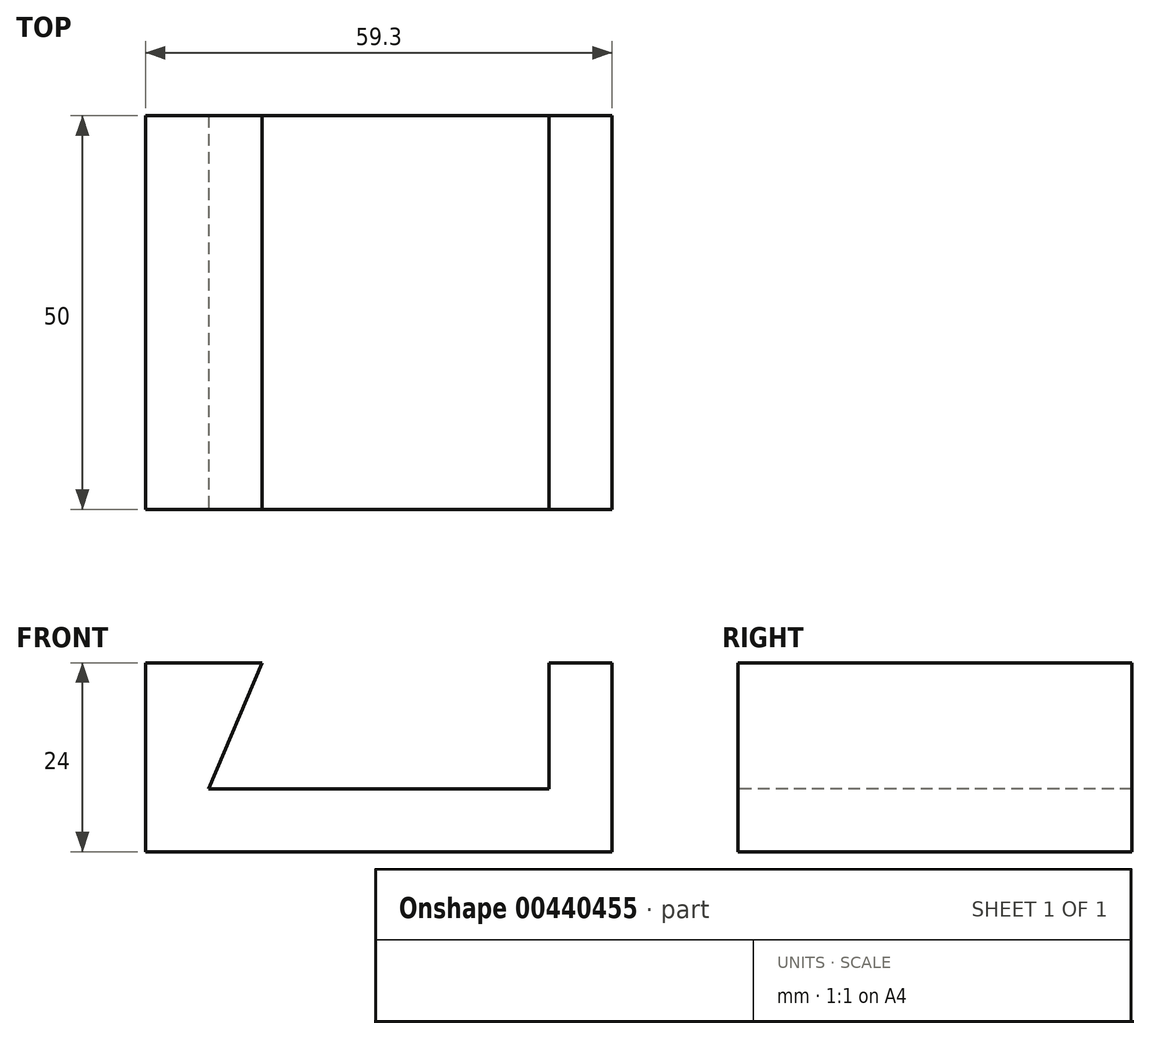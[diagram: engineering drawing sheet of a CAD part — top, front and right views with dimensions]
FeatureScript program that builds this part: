
annotation { "Feature Type Name" : "Feature", "Feature Type Description" : "" }
export const myFeature = defineFeature(function(context is Context, id is Id, definition is map)
    precondition{}
    {
        {
            var Q0;
            Q0=qCreatedBy(makeId("Top.planeOp"),FACE);
            var sketch = newSketch(context, id + "F0", { "sketchPlane" : qUnion([Q0])});
            skLineSegment(sketch, "E0.bottom", {"start": v(-26, 25) * mm, "end": v(33.3, 25) * mm});
            skLineSegment(sketch, "E0.top", {"start": v(-26, -25) * mm, "end": v(33.3, -25) * mm});
            skLineSegment(sketch, "E0.left", {"start": v(-26, 25) * mm, "end": v(-26, -25) * mm});
            skLineSegment(sketch, "E0.right", {"start": v(33.3, 25) * mm, "end": v(33.3, -25) * mm});
            skSolve(sketch);
        }
        {
            var Q0;
            Q0=makeQuery(id+"F0.imprint","IMPRINT",FACE,{"disambiguationData":[TD([[makeQuery(id+"F0.imprint","IMPRINT",EDGE,{"derivedFrom":sQuery(id+"F0.wireOp",EDGE,"E0.bottom")}),-1.0]])]});
            extrude(context, id + "F1", {"entities" : qUnion([Q0]), "endBound" : BoundingType.SYMMETRIC, "depth" : 24 * mm});
        }
        {
            var Q0;
            Q0=makeQuery(id+"F1.opExtrude","SWEPT_FACE",FACE,{"disambiguationData":[OSD([sQuery(id+"F0.wireOp",EDGE,"E0.top")])]});
            var sketch = newSketch(context, id + "F2", { "sketchPlane" : qUnion([Q0])});
            skLineSegment(sketch, "E1", {"start": v(-27.38, -4) * mm, "end": v(26.98, -4) * mm, "construction": true});
            skLineSegment(sketch, "E2", {"start": v(25.3, 17.12) * mm, "end": v(25.3, -18.4) * mm, "construction": true});
            skLineSegment(sketch, "E3", {"start": v(-18, 19.46) * mm, "end": v(-18, -16.16) * mm, "construction": true});
            skLineSegment(sketch, "E4", {"start": v(-11.2, 19.1) * mm, "end": v(-11.2, -16.2) * mm, "construction": true});
            skLineSegment(sketch, "E5", {"start": v(25.3, 12) * mm, "end": v(25.3, -4) * mm});
            skLineSegment(sketch, "E6", {"start": v(25.3, -4) * mm, "end": v(-18, -4) * mm});
            skLineSegment(sketch, "E7", {"start": v(-18, -4) * mm, "end": v(-11.2, 12) * mm});
            skLineSegment(sketch, "E8", {"start": v(-11.2, 12) * mm, "end": v(25.3, 12) * mm});
            skSolve(sketch);
        }
        {
            var Q0;
            Q0 = qSketchRegion(id + "F2", true);
            extrude(context, id + "F3", {"entities" : qUnion([Q0]), "operationType" : NewBodyOperationType.REMOVE, "oppositeDirection" : true, "depth" : 50 * mm});
        }
    });
